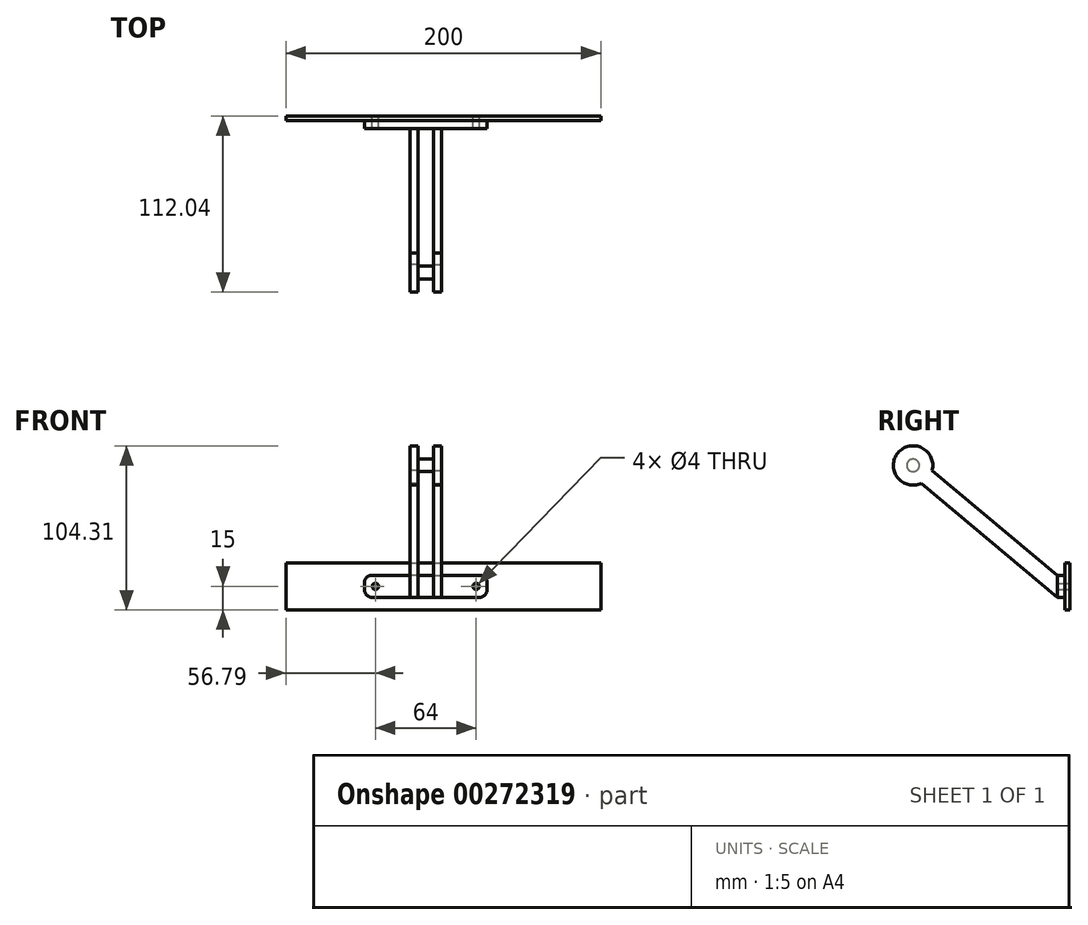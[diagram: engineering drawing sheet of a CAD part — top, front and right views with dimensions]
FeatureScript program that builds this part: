
annotation { "Feature Type Name" : "Feature", "Feature Type Description" : "" }
export const myFeature = defineFeature(function(context is Context, id is Id, definition is map)
    precondition{}
    {
        {
            var Q0;
            Q0=qCreatedBy(makeId("Front.planeOp"),FACE);
            var sketch = newSketch(context, id + "F0", { "sketchPlane" : qUnion([Q0])});
            skLineSegment(sketch, "E0.bottom", {"start": v(-88.79, 30) * mm, "end": v(111.21, 30) * mm});
            skLineSegment(sketch, "E0.top", {"start": v(-88.79, 0) * mm, "end": v(111.21, 0) * mm});
            skLineSegment(sketch, "E0.left", {"start": v(-88.79, 30) * mm, "end": v(-88.79, 0) * mm});
            skLineSegment(sketch, "E0.right", {"start": v(111.21, 30) * mm, "end": v(111.21, 0) * mm});
            skCircle(sketch, "E1", {"center": v(-32, 15) * mm, "radius": 2 * mm});
            skCircle(sketch, "E2", {"center": v(32, 15) * mm, "radius": 2 * mm});
            skLineSegment(sketch, "E3", {"start": v(-32, 15) * mm, "end": v(32, 15) * mm});
            skLineSegment(sketch, "E4", {"start": v(0, 0) * mm, "end": v(0, 30) * mm, "construction": true});
            skPoint(sketch, "E5", {"position": v(0, 15) * mm});
            skSolve(sketch);
        }
        {
            var Q0;
            Q0=makeQuery(id+"F0.imprint","IMPRINT",FACE,{"disambiguationData":[TD([[makeQuery(id+"F0.imprint","IMPRINT",EDGE,{"derivedFrom":sQuery(id+"F0.wireOp",EDGE,"E0.bottom")}),-1.0]])]});
            extrude(context, id + "F1", {"entities" : qUnion([Q0]), "depth" : 3 * mm, "offsetDistance" : 25 * mm});
        }
        {
            var Q0;
            Q0=makeQuery(id+"F1.opExtrude","CAP_FACE",FACE,{"disambiguationData":[OSD([sQuery(id+"F0.wireOp",EDGE,"E0.bottom"),sQuery(id+"F0.wireOp",EDGE,"E0.top"),sQuery(id+"F0.wireOp",EDGE,"E0.left"),sQuery(id+"F0.wireOp",EDGE,"E0.right"),sQuery(id+"F0.wireOp",EDGE,"E1"),sQuery(id+"F0.wireOp",EDGE,"E2")])],"isStart":false});
            var sketch = newSketch(context, id + "F2", { "sketchPlane" : qUnion([Q0])});
            skLineSegment(sketch, "E6.bottom", {"start": v(-39, 22) * mm, "end": v(39, 22) * mm});
            skLineSegment(sketch, "E6.top", {"start": v(-39, 8) * mm, "end": v(39, 8) * mm});
            skLineSegment(sketch, "E6.left", {"start": v(-39, 22) * mm, "end": v(-39, 8) * mm});
            skLineSegment(sketch, "E6.right", {"start": v(39, 22) * mm, "end": v(39, 8) * mm});
            skCircle(sketch, "E7.0", {"center": v(-32, 15) * mm, "radius": 2 * mm});
            skCircle(sketch, "E8.0", {"center": v(32, 15) * mm, "radius": 2 * mm});
            skSolve(sketch);
        }
        {
            var Q0;
            Q0=makeQuery(id+"F2.imprint","IMPRINT",FACE,{"disambiguationData":[TD([[makeQuery(id+"F2.imprint","IMPRINT",EDGE,{"derivedFrom":sQuery(id+"F2.wireOp",EDGE,"E6.bottom")}),-1.0]])]});
            extrude(context, id + "F3", {"entities" : qUnion([Q0]), "depth" : 5 * mm, "offsetDistance" : 25 * mm});
        }
        {
            var Q0;
            Q0=makeQuery(id+"F3.opExtrude","SWEPT_EDGE",EDGE,{"disambiguationData":[OSD([sQuery(id+"F2.wireOp",EDGE,"E6.bottom"),sQuery(id+"F2.wireOp",EDGE,"E6.left")])]});
            var Q1;
            Q1=makeQuery(id+"F3.opExtrude","SWEPT_EDGE",EDGE,{"disambiguationData":[OSD([sQuery(id+"F2.wireOp",EDGE,"E6.top"),sQuery(id+"F2.wireOp",EDGE,"E6.left")])]});
            var Q2;
            Q2=makeQuery(id+"F3.opExtrude","SWEPT_EDGE",EDGE,{"disambiguationData":[OSD([sQuery(id+"F2.wireOp",EDGE,"E6.top"),sQuery(id+"F2.wireOp",EDGE,"E6.right")])]});
            var Q3;
            Q3=makeQuery(id+"F3.opExtrude","SWEPT_EDGE",EDGE,{"disambiguationData":[OSD([sQuery(id+"F2.wireOp",EDGE,"E6.bottom"),sQuery(id+"F2.wireOp",EDGE,"E6.right")])]});
            fillet(context, id + "F4", {"entities" : qUnion([Q0, Q1, Q2, Q3]), "radius" : 5 * mm, "tangentPropagation" : true, "allowEdgeOverflow" : false});
        }
        {
            var Q0;
            Q0=qCreatedBy(makeId("Right.planeOp"),FACE);
            cPlane(context, id + "F5", {"entities" : qUnion([Q0]), "cplaneType" : CPlaneType.OFFSET, "offset" : 10 * mm, "oppositeDirection" : true, "width" : 150 * mm, "height" : 150 * mm});
        }
        {
            var Q0;
            Q0=qCreatedBy(id+"F5.planeOp",FACE);
            var sketch = newSketch(context, id + "F6", { "sketchPlane" : qUnion([Q0])});
            skLineSegment(sketch, "E9", {"start": v(-8, 22) * mm, "end": v(-99.93, 99.13) * mm});
            skLineSegment(sketch, "E10", {"start": v(-8, 8) * mm, "end": v(-106.82, 90.92) * mm});
            skLineSegment(sketch, "E11", {"start": v(-8, 8) * mm, "end": v(-8, 22) * mm});
            skLineSegment(sketch, "E12", {"start": v(-96.1, 95.92) * mm, "end": v(-102.99, 87.7) * mm, "construction": true});
            skCircle(sketch, "E13", {"center": v(-99.54, 91.81) * mm, "radius": 12.5 * mm});
            skCircle(sketch, "E14", {"center": v(-99.54, 91.81) * mm, "radius": 4 * mm});
            skLineSegment(sketch, "E15.trimOffspring", {"start": v(-99.93, 99.13) * mm, "end": v(-106.82, 90.92) * mm});
            skPoint(sketch, "E16.start.orphan", {"position": v(-81.2, 135.22) * mm});
            skSolve(sketch);
        }
        {
            var Q0;
            {var subQ0=sQuery(id+"F6.wireOp",EDGE,"E11");Q0=makeQuery(id+"F6.imprint","IMPRINT",FACE,{"disambiguationData":[TD([[makeQuery(id+"F6.imprint","IMPRINT",EDGE,{"derivedFrom":subQ0}),1.0]])]});}
            var Q1;
            Q1=makeQuery(id+"F6.imprint","IMPRINT",FACE,{"disambiguationData":[TD([[makeQuery(id+"F6.imprint","IMPRINT",EDGE,{"derivedFrom":sQuery(id+"F6.wireOp",EDGE,"E14")}),-1.0]])]});
            var Q2;
            {var subQ0=sQuery(id+"F6.wireOp",EDGE,"E15.trimOffspring");Q2=makeQuery(id+"F6.imprint","IMPRINT",FACE,{"disambiguationData":[TD([[makeQuery(id+"F6.imprint","IMPRINT",EDGE,{"derivedFrom":subQ0}),-1.0]])]});}
            var Q3;
            Q3=makeQuery(id+"F6.imprint","IMPRINT",FACE,{"disambiguationData":[TD([[makeQuery(id+"F6.imprint","IMPRINT",EDGE,{"derivedFrom":sQuery(id+"F6.wireOp",EDGE,"E14")}),1.0]])]});
            extrude(context, id + "F7", {"entities" : qUnion([Q0, Q1, Q2, Q3]), "depth" : 5 * mm, "offsetDistance" : 25 * mm});
        }
        {
            var Q0;
            Q0=makeQuery(id+"F7.opExtrude","SWEPT_BODY",BODY,{"disambiguationData":[OSD([sQuery(id+"F6.wireOp",EDGE,"E9"),sQuery(id+"F6.wireOp",EDGE,"E10"),sQuery(id+"F6.wireOp",EDGE,"E11"),sQuery(id+"F6.wireOp",EDGE,"E13")])]});
            var Q1;
            Q1=qCreatedBy(makeId("Right.planeOp"),FACE);
            mirror(context, id + "F8", {"operationType" : NewBodyOperationType.ADD, "entities" : qUnion([Q0]), "mirrorPlane" : qUnion([Q1])});
        }
        {
            var Q0;
            Q0=makeQuery(id+"F6.imprint","IMPRINT",FACE,{"disambiguationData":[TD([[makeQuery(id+"F6.imprint","IMPRINT",EDGE,{"derivedFrom":sQuery(id+"F6.wireOp",EDGE,"E14")}),1.0]])]});
            var Q1;
            Q1=makeQuery(id+"F8.opPattern","COPY",FACE,{"derivedFrom":makeQuery(id+"F7.opExtrude","CAP_FACE",FACE,{"disambiguationData":[OSD([sQuery(id+"F6.wireOp",EDGE,"E9"),sQuery(id+"F6.wireOp",EDGE,"E10"),sQuery(id+"F6.wireOp",EDGE,"E11"),sQuery(id+"F6.wireOp",EDGE,"E13")])],"isStart":false}),"instanceName":"1"});
            extrude(context, id + "F9", {"entities" : qUnion([Q0]), "operationType" : NewBodyOperationType.ADD, "endBound" : BoundingType.UP_TO_SURFACE, "depth" : 25 * mm, "endBoundEntityFace" : qUnion([Q1]), "offsetDistance" : 25 * mm});
        }
    });
